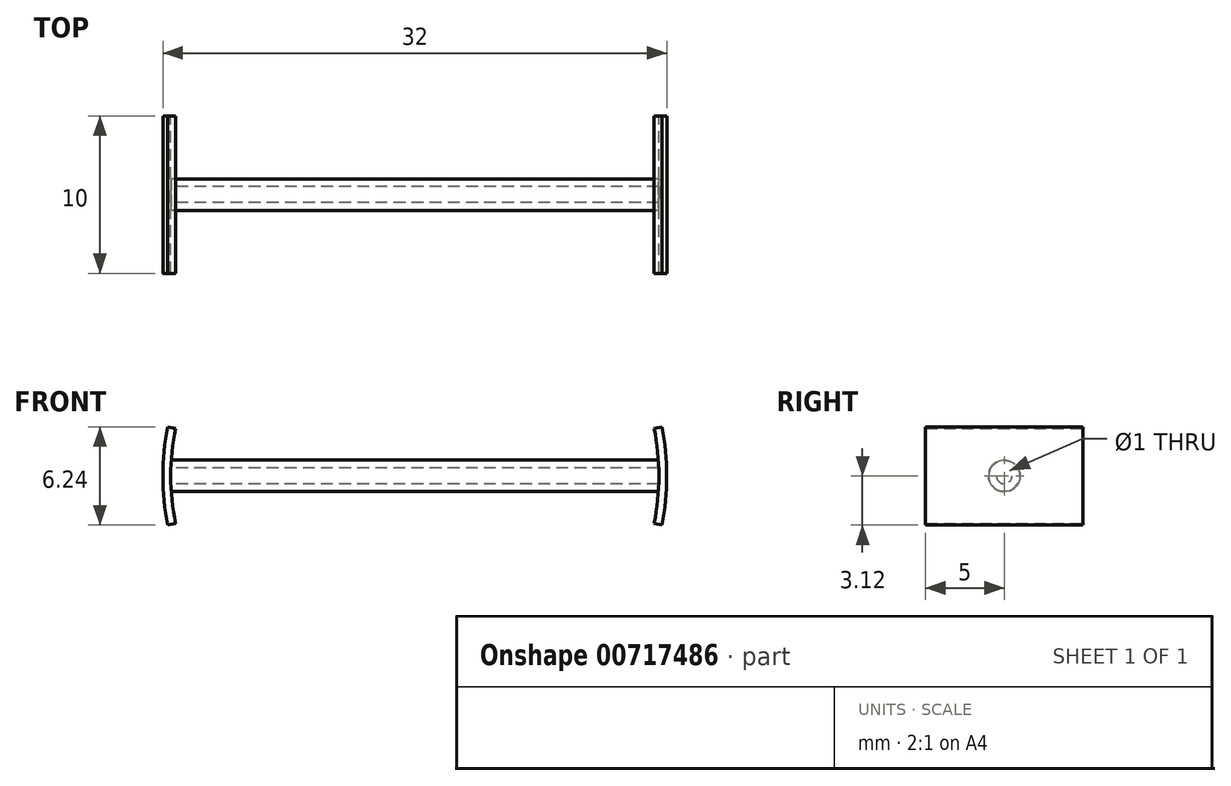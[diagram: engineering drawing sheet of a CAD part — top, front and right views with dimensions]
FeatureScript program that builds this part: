
annotation { "Feature Type Name" : "Feature", "Feature Type Description" : "" }
export const myFeature = defineFeature(function(context is Context, id is Id, definition is map)
    precondition{}
    {
        {
            var Q0;
            Q0=qCreatedBy(makeId("Right.planeOp"),FACE);
            var sketch = newSketch(context, id + "F0", { "sketchPlane" : qUnion([Q0])});
            skCircle(sketch, "E0", {"center": v(0, 0) * mm, "radius": 1 * mm});
            skCircle(sketch, "E1", {"center": v(0, 0) * mm, "radius": 0.5 * mm});
            skSolve(sketch);
        }
        {
            var Q0;
            Q0=makeQuery(id+"F0.imprint","IMPRINT",FACE,{"disambiguationData":[TD([[makeQuery(id+"F0.imprint","IMPRINT",EDGE,{"derivedFrom":sQuery(id+"F0.wireOp",EDGE,"E0")}),1.0]])]});
            extrude(context, id + "F1", {"entities" : qUnion([Q0]), "endBound" : BoundingType.SYMMETRIC, "depth" : 31 * mm, "offsetDistance" : 25 * mm});
        }
        {
            var Q0;
            Q0=qCreatedBy(makeId("Front.planeOp"),FACE);
            var sketch = newSketch(context, id + "F2", { "sketchPlane" : qUnion([Q0])});
            skPoint(sketch, "E2.center", {"position": v(0, 0) * mm});
            skArc(sketch, "E3.trimOffspring", {"start": v(15.2, -3.02) * mm, "mid": v(15.5, 0) * mm, "end": v(15.2, 3.02) * mm});
            skArc(sketch, "E4.trimOffspring", {"start": v(15.7, -3.12) * mm, "mid": v(16, 0) * mm, "end": v(15.7, 3.12) * mm});
            skArc(sketch, "E5.trimOffspring", {"start": v(-15.2, 3.02) * mm, "mid": v(-15.5, 0) * mm, "end": v(-15.2, -3.02) * mm});
            skArc(sketch, "E6.trimOffspring", {"start": v(-15.7, 3.12) * mm, "mid": v(-16, 0) * mm, "end": v(-15.7, -3.12) * mm});
            skLineSegment(sketch, "E7", {"start": v(15.2, -3.02) * mm, "end": v(15.7, -3.12) * mm});
            skLineSegment(sketch, "E8", {"start": v(15.2, 3.02) * mm, "end": v(15.7, 3.12) * mm});
            skLineSegment(sketch, "E9", {"start": v(-15.2, 3.02) * mm, "end": v(-15.7, 3.12) * mm});
            skLineSegment(sketch, "E10", {"start": v(-15.2, -3.02) * mm, "end": v(-15.7, -3.12) * mm});
            skSolve(sketch);
        }
        {
            var Q0;
            Q0=makeQuery(id+"F2.imprint","IMPRINT",FACE,{"disambiguationData":[TD([[makeQuery(id+"F2.imprint","IMPRINT",EDGE,{"derivedFrom":sQuery(id+"F2.wireOp",EDGE,"E3.trimOffspring")}),-1.0]])]});
            var Q1;
            Q1=makeQuery(id+"F2.imprint","IMPRINT",FACE,{"disambiguationData":[TD([[makeQuery(id+"F2.imprint","IMPRINT",EDGE,{"derivedFrom":sQuery(id+"F2.wireOp",EDGE,"E5.trimOffspring")}),-1.0]])]});
            extrude(context, id + "F3", {"entities" : qUnion([Q0, Q1]), "operationType" : NewBodyOperationType.ADD, "endBound" : BoundingType.SYMMETRIC, "depth" : 10 * mm, "offsetDistance" : 25 * mm});
        }
    });
